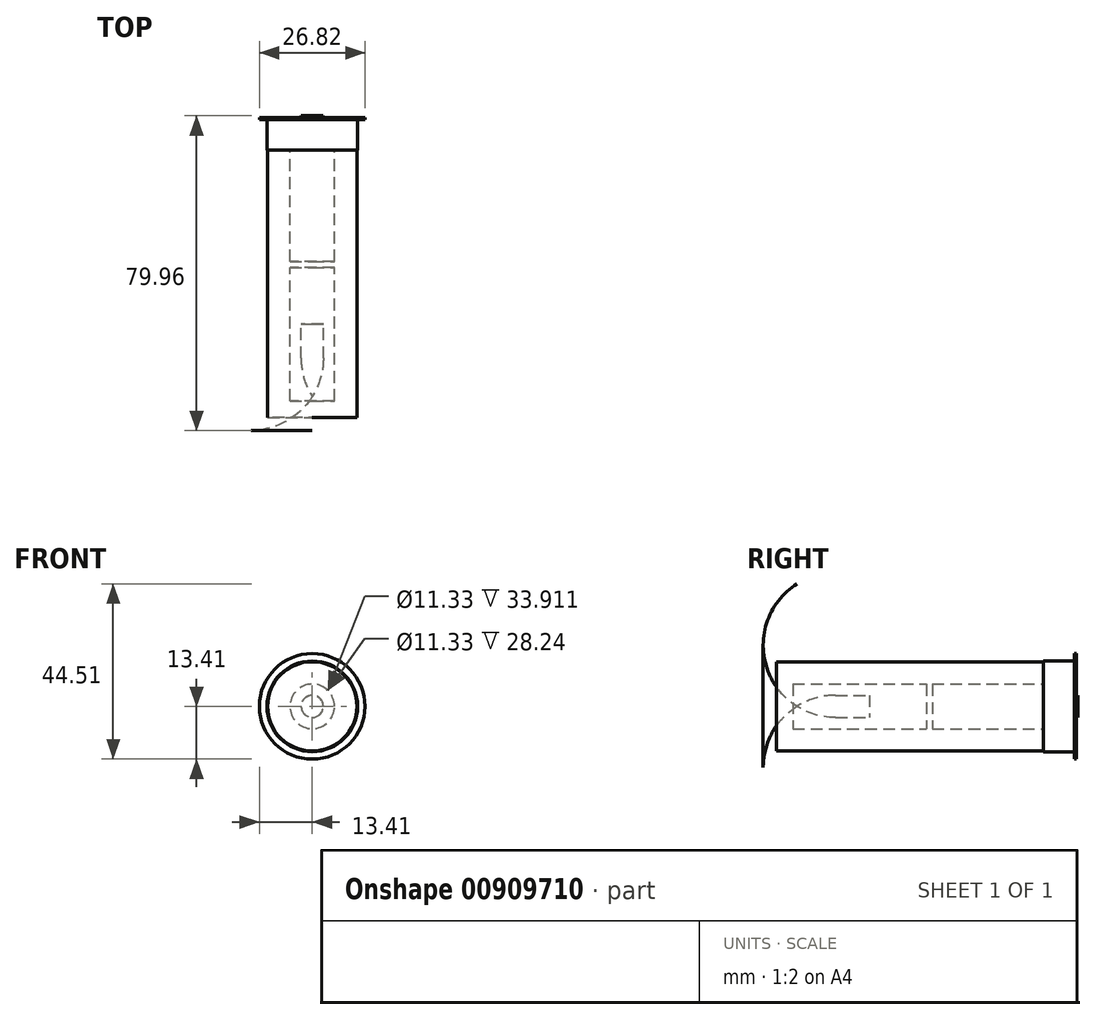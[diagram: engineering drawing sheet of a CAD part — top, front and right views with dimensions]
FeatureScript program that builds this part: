
annotation { "Feature Type Name" : "Feature", "Feature Type Description" : "" }
export const myFeature = defineFeature(function(context is Context, id is Id, definition is map)
    precondition{}
    {
        {
            var Q0;
            Q0=qCreatedBy(makeId("Top.planeOp"),FACE);
            var sketch = newSketch(context, id + "F0", { "sketchPlane" : qUnion([Q0])});
            skLineSegment(sketch, "E0", {"start": v(0, 0) * mm, "end": v(11.33, 0) * mm});
            skLineSegment(sketch, "E1", {"start": v(13.4, 76.2) * mm, "end": v(13.4, 75.7) * mm});
            skLineSegment(sketch, "E2", {"start": v(0, 0) * mm, "end": v(0, 4.19) * mm});
            skLineSegment(sketch, "E3", {"start": v(0, 4.19) * mm, "end": v(5.67, 4.19) * mm});
            skLineSegment(sketch, "E4", {"start": v(0, 38.1) * mm, "end": v(5.67, 38.1) * mm});
            skLineSegment(sketch, "E5", {"start": v(5.67, 38.1) * mm, "end": v(5.67, 4.19) * mm});
            skLineSegment(sketch, "E6", {"start": v(0, 76.2) * mm, "end": v(0, 76.63) * mm});
            skLineSegment(sketch, "E7", {"start": v(0, 76.63) * mm, "end": v(2.78, 76.63) * mm});
            skLineSegment(sketch, "E8", {"start": v(2.78, 76.63) * mm, "end": v(2.78, 76.2) * mm});
            skLineSegment(sketch, "E9", {"start": v(2.78, 76.2) * mm, "end": v(13.4, 76.2) * mm});
            skLineSegment(sketch, "E10", {"start": v(5.67, 39.61) * mm, "end": v(0, 39.61) * mm});
            skLineSegment(sketch, "E11", {"start": v(5.67, 67.85) * mm, "end": v(0, 67.85) * mm});
            skLineSegment(sketch, "E12", {"start": v(0, 76.2) * mm, "end": v(0, 67.85) * mm});
            skLineSegment(sketch, "E13", {"start": v(0, 38.1) * mm, "end": v(0, 39.61) * mm});
            skLineSegment(sketch, "E14", {"start": v(5.67, 67.85) * mm, "end": v(5.67, 39.61) * mm});
            skLineSegment(sketch, "E15", {"start": v(11.51, 67.85) * mm, "end": v(11.33, 67.85) * mm});
            skLineSegment(sketch, "E16", {"start": v(11.51, 67.85) * mm, "end": v(11.51, 75.7) * mm});
            skLineSegment(sketch, "E17", {"start": v(11.51, 75.7) * mm, "end": v(13.4, 75.7) * mm});
            skLineSegment(sketch, "E18", {"start": v(11.33, 67.85) * mm, "end": v(11.33, 0) * mm});
            skSolve(sketch);
        }
        {
            var Q0;
            Q0=qCreatedBy(makeId("Top.planeOp"),FACE);
            var sketch = newSketch(context, id + "F1", { "sketchPlane" : qUnion([Q0])});
            skLineSegment(sketch, "E19", {"start": v(0, 23.67) * mm, "end": v(0, 5.25) * mm});
            skLineSegment(sketch, "E20", {"start": v(0, 23.67) * mm, "end": v(2.83, 23.67) * mm});
            skLineSegment(sketch, "E21", {"start": v(2.83, 23.67) * mm, "end": v(2.83, 15.06) * mm});
            skArc(sketch, "E22", {"start": v(0, 5.25) * mm, "mid": v(2.1, 9.96) * mm, "end": v(2.83, 15.06) * mm});
            skSolve(sketch);
        }
        {
            var Q0;
            Q0=makeQuery(id+"F1.imprint","IMPRINT",FACE,{"disambiguationData":[TD([[makeQuery(id+"F1.imprint","IMPRINT",EDGE,{"derivedFrom":sQuery(id+"F1.wireOp",EDGE,"E19")}),1.0]])]});
            var Q1;
            Q1=sQuery(id+"F1.wireOp",EDGE,"E19");
            revolve(context, id + "F2", {"surfaceOperationType" : NewSurfaceOperationType.NEW, "entities" : qUnion([Q0]), "axis" : qUnion([Q1]), "revolveType" : RevolveType.FULL});
        }
        {
            var Q0;
            Q0=makeQuery(id+"F0.imprint","IMPRINT",FACE,{"disambiguationData":[TD([[makeQuery(id+"F0.imprint","IMPRINT",EDGE,{"derivedFrom":sQuery(id+"F0.wireOp",EDGE,"E0")}),1.0]])]});
            var Q1;
            Q1=sQuery(id+"F0.wireOp",EDGE,"E12");
            revolve(context, id + "F3", {"surfaceOperationType" : NewSurfaceOperationType.NEW, "entities" : qUnion([Q0]), "axis" : qUnion([Q1]), "revolveType" : RevolveType.FULL});
        }
    });
